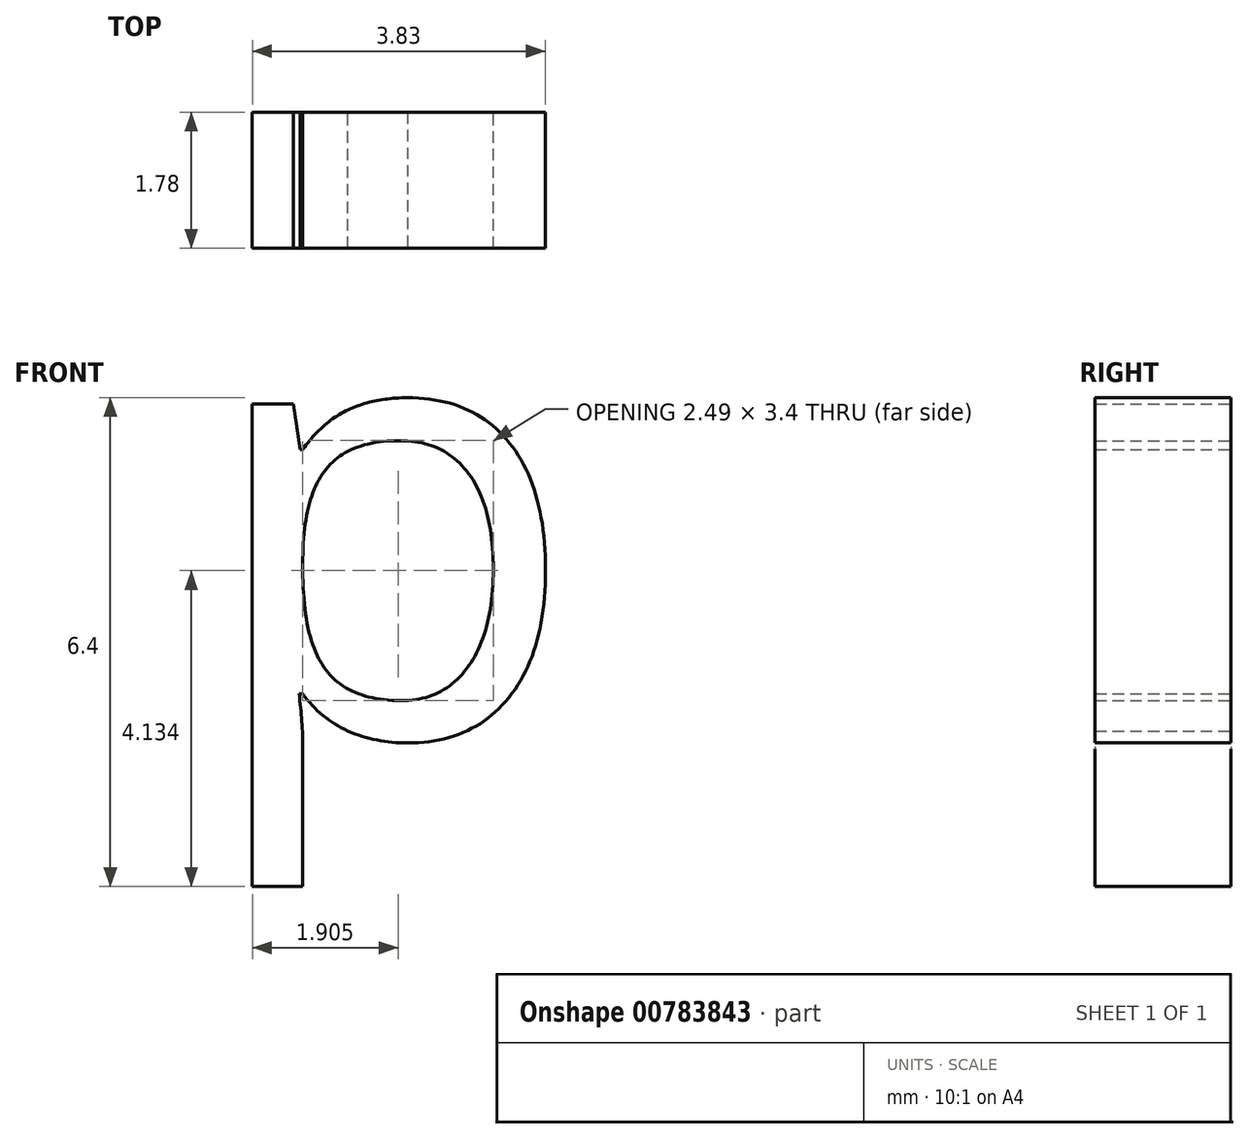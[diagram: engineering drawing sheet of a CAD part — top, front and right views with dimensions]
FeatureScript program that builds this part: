
annotation { "Feature Type Name" : "Feature", "Feature Type Description" : "" }
export const myFeature = defineFeature(function(context is Context, id is Id, definition is map)
    precondition{}
    {
        {
            var Q0;
            Q0=qCreatedBy(makeId("Front.planeOp"),FACE);
            var sketch = newSketch(context, id + "F0", { "sketchPlane" : qUnion([Q0])});
            skText(sketch, "E0", { "text": "p", "fontName": "OpenSans-Regular.ttf"});
            const initialGuessF0  = {"E0": [-0.06394, 0.04886, 1, 0, 0.00586]};
            skSetInitialGuess(sketch, initialGuessF0);
            skSolve(sketch);
        }
        {
            var Q0;
            Q0 = qSketchRegion(id + "F0", true);
            extrude(context, id + "F1", {"entities" : qUnion([Q0]), "depth" : 1.78 * mm, "offsetDistance" : 25.4 * mm});
        }
    });
